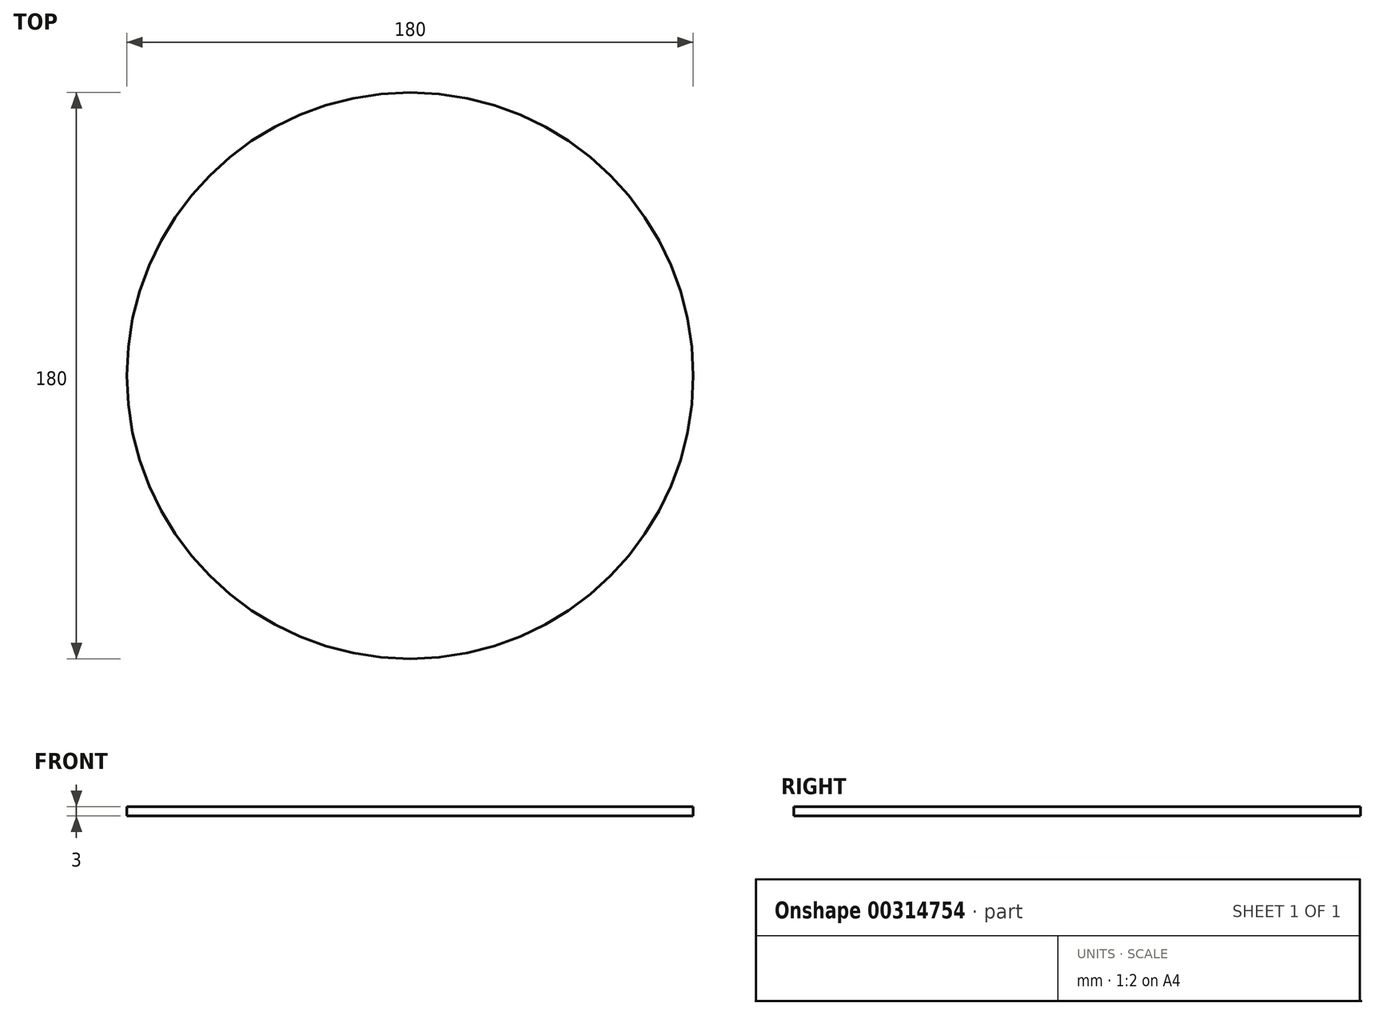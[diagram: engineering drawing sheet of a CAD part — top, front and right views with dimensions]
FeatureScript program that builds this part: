
annotation { "Feature Type Name" : "Feature", "Feature Type Description" : "" }
export const myFeature = defineFeature(function(context is Context, id is Id, definition is map)
    precondition{}
    {
        {
            var Q0;
            Q0=qCreatedBy(makeId("Top.planeOp"),FACE);
            var sketch = newSketch(context, id + "F0", { "sketchPlane" : qUnion([Q0])});
            skCircle(sketch, "E0", {"center": v(0, 0) * mm, "radius": 90 * mm});
            skLineSegment(sketch, "E1", {"start": v(0, 0) * mm, "end": v(90, 0) * mm});
            skSolve(sketch);
        }
        {
            var Q0;
            Q0=makeQuery(id+"F0.imprint","IMPRINT",FACE,{"disambiguationData":[TD([[makeQuery(id+"F0.imprint","IMPRINT",EDGE,{"derivedFrom":sQuery(id+"F0.wireOp",EDGE,"E0")}),1.0]])]});
            extrude(context, id + "F1", {"entities" : qUnion([Q0]), "depth" : 3 * mm});
        }
    });
